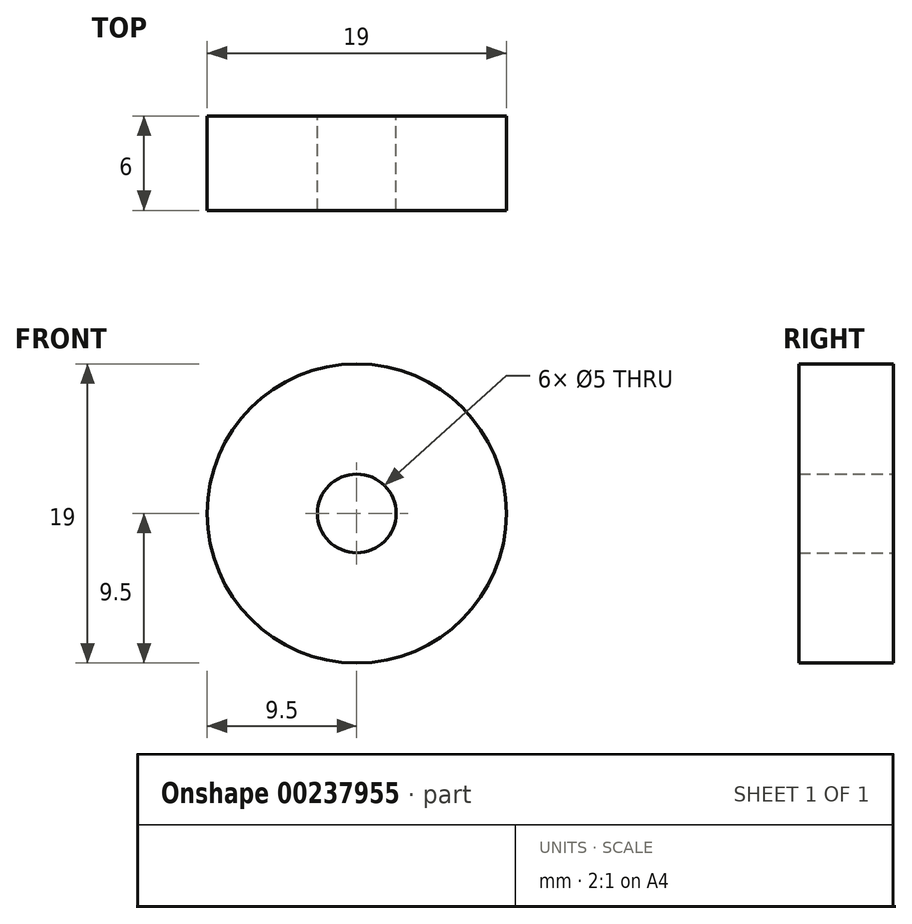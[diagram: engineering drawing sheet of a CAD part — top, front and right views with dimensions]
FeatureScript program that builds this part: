
annotation { "Feature Type Name" : "Feature", "Feature Type Description" : "" }
export const myFeature = defineFeature(function(context is Context, id is Id, definition is map)
    precondition{}
    {
        {
            var Q0;
            Q0=qCreatedBy(makeId("Front.planeOp"),FACE);
            var sketch = newSketch(context, id + "F0", { "sketchPlane" : qUnion([Q0])});
            skCircle(sketch, "E0", {"center": v(0, 0) * mm, "radius": 9.5 * mm});
            skCircle(sketch, "E1", {"center": v(0, 0) * mm, "radius": 2.5 * mm});
            skSolve(sketch);
        }
        {
            var Q0;
            Q0 = qSketchRegion(id + "F0", true);
            extrude(context, id + "F1", {"entities" : qUnion([Q0]), "depth" : 6 * mm});
        }
    });
